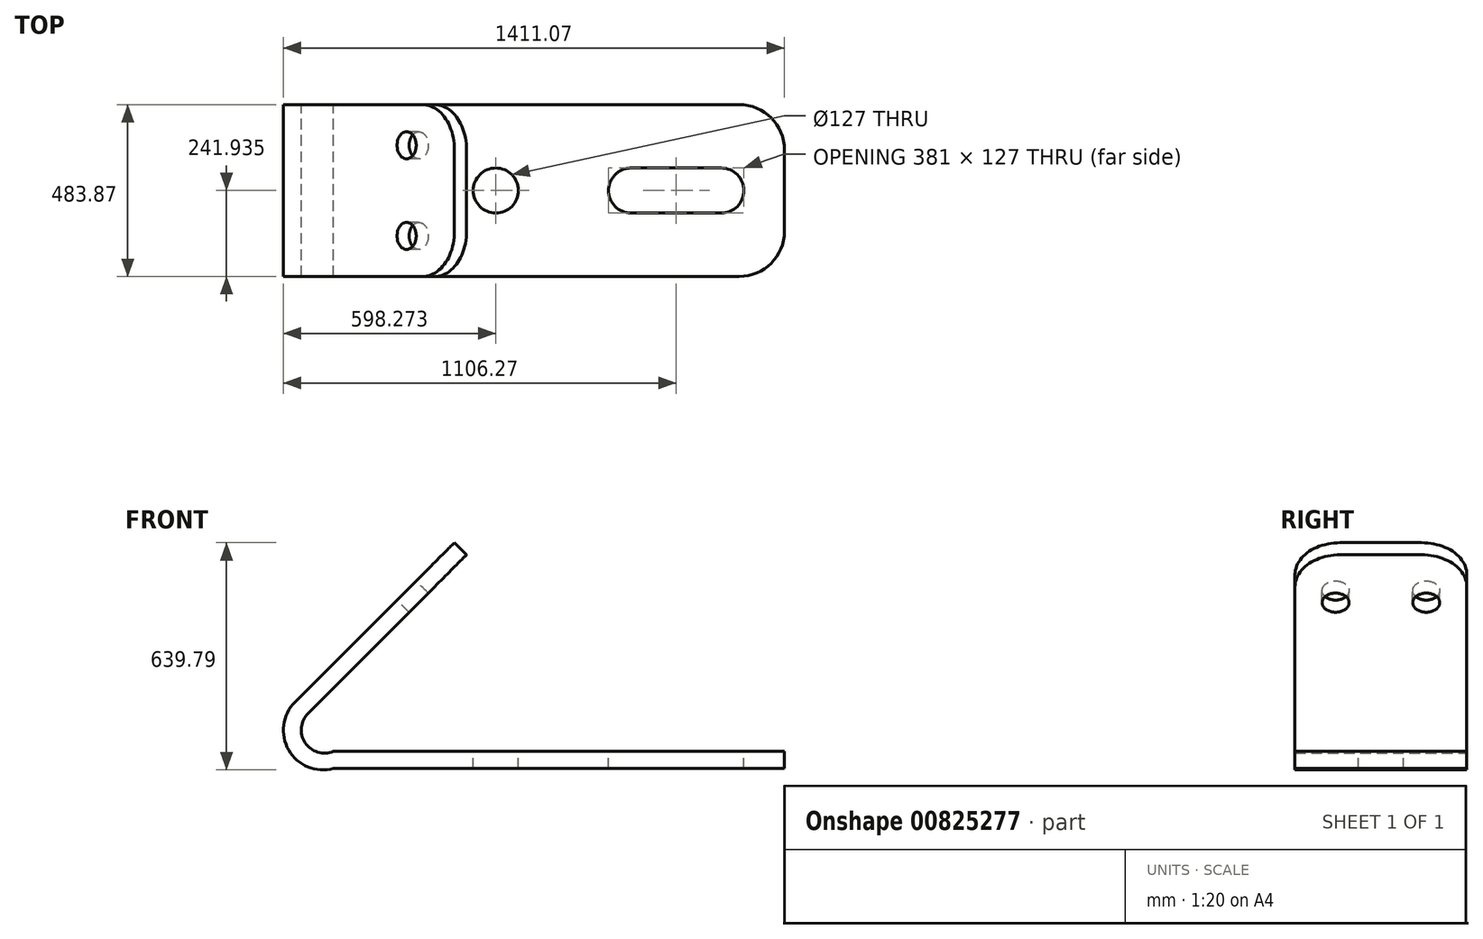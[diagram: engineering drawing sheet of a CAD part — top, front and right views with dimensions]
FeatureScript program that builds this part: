
annotation { "Feature Type Name" : "Feature", "Feature Type Description" : "" }
export const myFeature = defineFeature(function(context is Context, id is Id, definition is map)
    precondition{}
    {
        {
            var Q0;
            Q0=qCreatedBy(makeId("Front.planeOp"),FACE);
            var sketch = newSketch(context, id + "F0", { "sketchPlane" : qUnion([Q0])});
            skLineSegment(sketch, "E0", {"start": v(96, 277.08) * mm, "end": v(130.13, 242.96) * mm});
            skLineSegment(sketch, "E1", {"start": v(96, 277.08) * mm, "end": v(-353, -171.93) * mm});
            skArc(sketch, "E2", {"start": v(-353, -171.93) * mm, "mid": v(-370.66, -307) * mm, "end": v(-244.67, -358.8) * mm});
            skLineSegment(sketch, "E3", {"start": v(-244.67, -358.8) * mm, "end": v(1025.33, -358.8) * mm});
            skLineSegment(sketch, "E4", {"start": v(1025.33, -358.8) * mm, "end": v(1025.33, -310.54) * mm});
            skLineSegment(sketch, "E5", {"start": v(1025.33, -310.54) * mm, "end": v(-244.67, -310.54) * mm});
            skLineSegment(sketch, "E6", {"start": v(130.13, 242.96) * mm, "end": v(-316.2, -203.38) * mm});
            skArc(sketch, "E7", {"start": v(-316.2, -203.38) * mm, "mid": v(-324.4, -286.3) * mm, "end": v(-244.67, -310.54) * mm});
            skSolve(sketch);
        }
        {
            var Q0;
            Q0=makeQuery(id+"F0.imprint","IMPRINT",FACE,{"disambiguationData":[TD([[makeQuery(id+"F0.imprint","IMPRINT",EDGE,{"derivedFrom":sQuery(id+"F0.wireOp",EDGE,"E0")}),-1.0]])]});
            extrude(context, id + "F1", {"entities" : qUnion([Q0]), "depth" : 483.87 * mm, "offsetDistance" : 25.4 * mm});
        }
        {
            var Q0;
            Q0=makeQuery(id+"F1.opExtrude","SWEPT_FACE",FACE,{"disambiguationData":[OSD([sQuery(id+"F0.wireOp",EDGE,"E5")])]});
            var sketch = newSketch(context, id + "F2", { "sketchPlane" : qUnion([Q0])});
            skCircle(sketch, "E8", {"center": v(212.53, -241.94) * mm, "radius": 63.5 * mm});
            skArc(sketch, "E9", {"start": v(593.53, -178.44) * mm, "mid": v(548.63, -197.02) * mm, "end": v(530.03, -241.91) * mm});
            skArc(sketch, "E10", {"start": v(530.03, -241.91) * mm, "mid": v(548.63, -286.82) * mm, "end": v(593.53, -305.44) * mm});
            skArc(sketch, "E11", {"start": v(911.03, -241.94) * mm, "mid": v(892.43, -197.03) * mm, "end": v(847.53, -178.43) * mm});
            skArc(sketch, "E12", {"start": v(847.53, -305.44) * mm, "mid": v(892.43, -286.84) * mm, "end": v(911.03, -241.94) * mm});
            skLineSegment(sketch, "E13", {"start": v(593.53, -178.44) * mm, "end": v(847.53, -178.43) * mm});
            skLineSegment(sketch, "E14", {"start": v(593.53, -305.44) * mm, "end": v(847.53, -305.44) * mm});
            skSolve(sketch);
        }
        {
            var Q0;
            Q0=makeQuery(id+"F2.imprint","IMPRINT",FACE,{"disambiguationData":[TD([[makeQuery(id+"F2.imprint","IMPRINT",EDGE,{"derivedFrom":sQuery(id+"F2.wireOp",EDGE,"E8")}),1.0]])]});
            extrude(context, id + "F3", {"entities" : qUnion([Q0]), "operationType" : NewBodyOperationType.REMOVE, "endBound" : BoundingType.THROUGH_ALL, "oppositeDirection" : true, "depth" : 25.4 * mm, "offsetDistance" : 25.4 * mm});
        }
        {
            var Q0;
            Q0=makeQuery(id+"F1.opExtrude","SWEPT_FACE",FACE,{"disambiguationData":[OSD([sQuery(id+"F0.wireOp",EDGE,"E1")])]});
            var sketch = newSketch(context, id + "F4", { "sketchPlane" : qUnion([Q0])});
            skCircle(sketch, "E15", {"center": v(114.3, 73.32) * mm, "radius": 38.1 * mm});
            skCircle(sketch, "E16", {"center": v(369.57, 73.32) * mm, "radius": 38.1 * mm});
            skSolve(sketch);
        }
        {
            var Q0;
            Q0=makeQuery(id+"F4.imprint","IMPRINT",FACE,{"disambiguationData":[TD([[makeQuery(id+"F4.imprint","IMPRINT",EDGE,{"derivedFrom":sQuery(id+"F4.wireOp",EDGE,"E15")}),1.0]])]});
            var Q1;
            Q1=makeQuery(id+"F4.imprint","IMPRINT",FACE,{"disambiguationData":[TD([[makeQuery(id+"F4.imprint","IMPRINT",EDGE,{"derivedFrom":sQuery(id+"F4.wireOp",EDGE,"E16")}),1.0]])]});
            extrude(context, id + "F5", {"entities" : qUnion([Q0, Q1]), "operationType" : NewBodyOperationType.REMOVE, "oppositeDirection" : true, "depth" : 50.8 * mm, "offsetDistance" : 25.4 * mm});
        }
        {
            var Q0;
            Q0=makeQuery(id+"F1.opExtrude","CAP_EDGE",EDGE,{"disambiguationData":[OSD([sQuery(id+"F0.wireOp",EDGE,"E0")])],"isStart":true});
            var Q1;
            Q1=makeQuery(id+"F1.opExtrude","CAP_EDGE",EDGE,{"disambiguationData":[OSD([sQuery(id+"F0.wireOp",EDGE,"E0")])],"isStart":false});
            fillet(context, id + "F6", {"entities" : qUnion([Q0, Q1]), "radius" : 127 * mm, "tangentPropagation" : true, "allowEdgeOverflow" : false});
        }
        {
            var Q0;
            Q0=makeQuery(id+"F1.opExtrude","CAP_EDGE",EDGE,{"disambiguationData":[OSD([sQuery(id+"F0.wireOp",EDGE,"E4")])],"isStart":true});
            var Q1;
            Q1=makeQuery(id+"F1.opExtrude","CAP_EDGE",EDGE,{"disambiguationData":[OSD([sQuery(id+"F0.wireOp",EDGE,"E4")])],"isStart":false});
            fillet(context, id + "F7", {"entities" : qUnion([Q0, Q1]), "radius" : 127 * mm, "tangentPropagation" : true, "allowEdgeOverflow" : false});
        }
        {
            var Q0;
            Q0=makeQuery(id+"F2.imprint","IMPRINT",FACE,{"disambiguationData":[TD([[makeQuery(id+"F2.imprint","IMPRINT",EDGE,{"derivedFrom":sQuery(id+"F2.wireOp",EDGE,"E9")}),1.0]])]});
            extrude(context, id + "F8", {"entities" : qUnion([Q0]), "operationType" : NewBodyOperationType.REMOVE, "endBound" : BoundingType.THROUGH_ALL, "oppositeDirection" : true, "depth" : 25.4 * mm, "offsetDistance" : 25.4 * mm});
        }
    });
